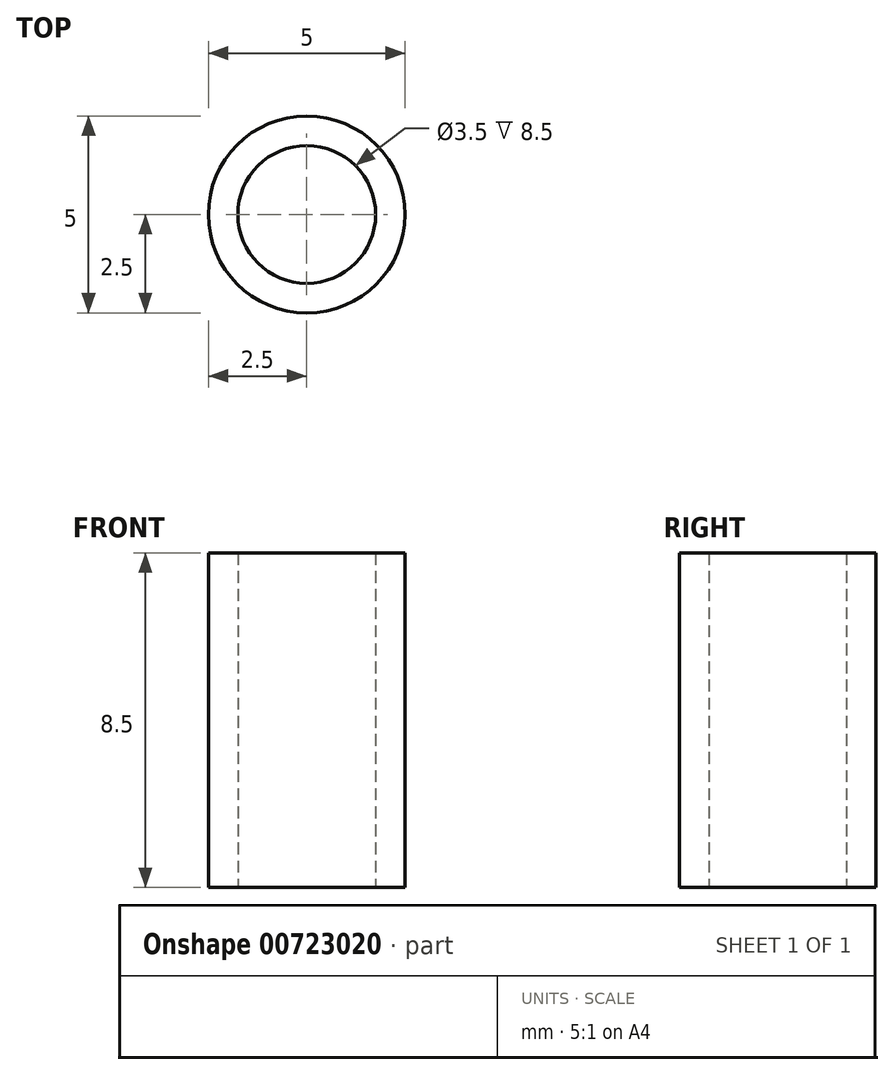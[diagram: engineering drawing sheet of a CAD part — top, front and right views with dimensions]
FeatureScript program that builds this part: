
annotation { "Feature Type Name" : "Feature", "Feature Type Description" : "" }
export const myFeature = defineFeature(function(context is Context, id is Id, definition is map)
    precondition{}
    {
        {
            var Q0;
            Q0=qCreatedBy(makeId("Top.planeOp"),FACE);
            var sketch = newSketch(context, id + "F0", { "sketchPlane" : qUnion([Q0])});
            skCircle(sketch, "E0", {"center": v(0, 0) * mm, "radius": 2.5 * mm});
            skCircle(sketch, "E1", {"center": v(0, 0) * mm, "radius": 1.75 * mm});
            skSolve(sketch);
        }
        {
            var Q0;
            Q0 = qSketchRegion(id + "F0", true);
            extrude(context, id + "F1", {"entities" : qUnion([Q0]), "depth" : 8.5 * mm, "offsetDistance" : 25 * mm});
        }
    });
